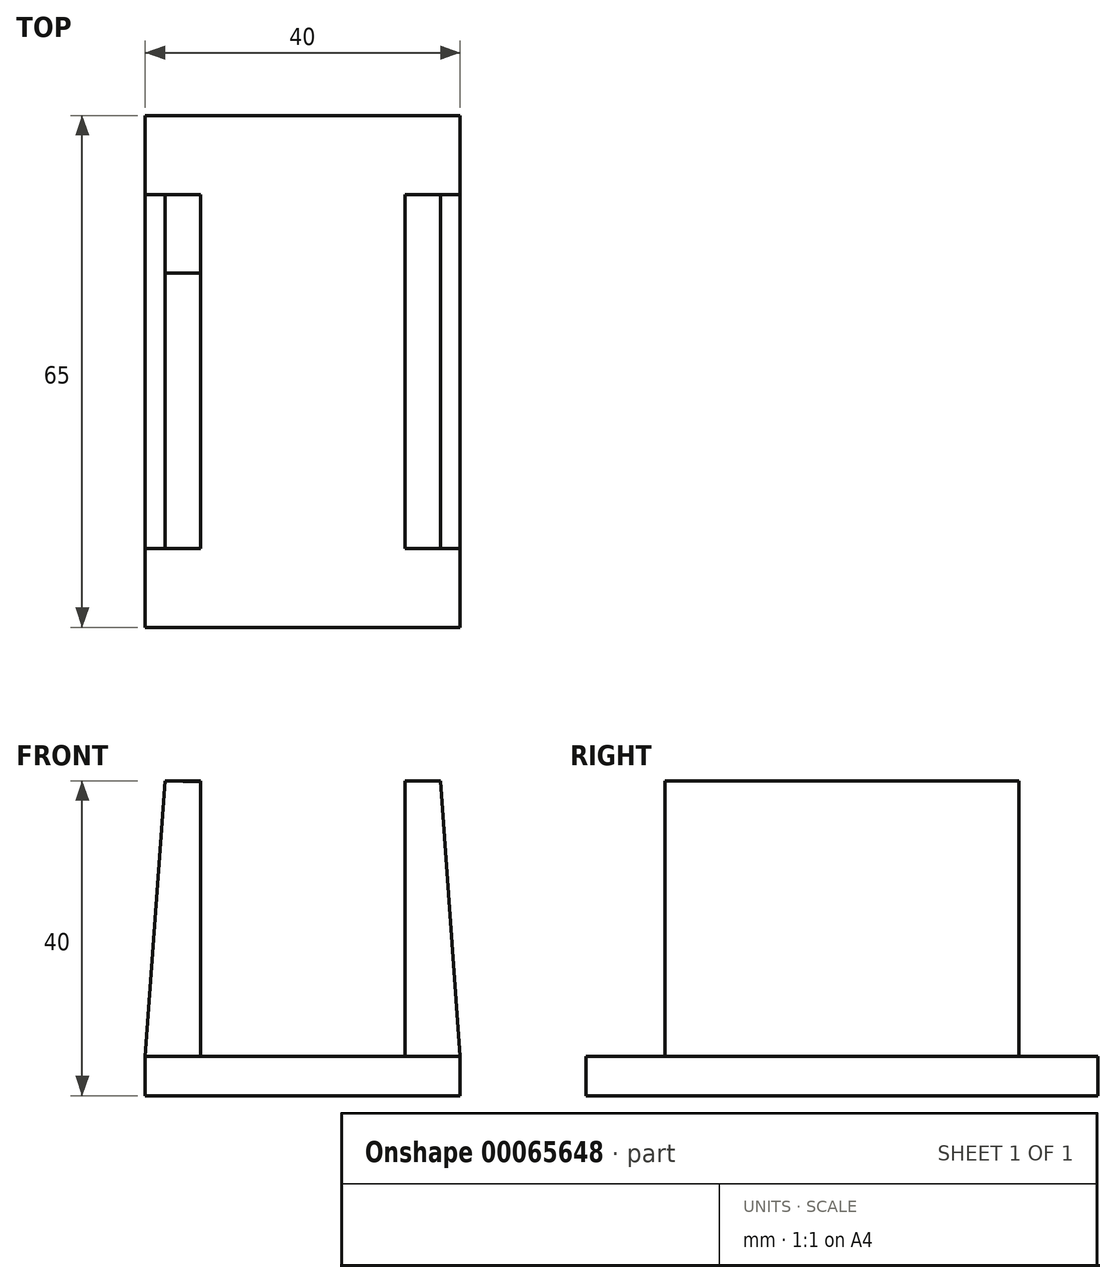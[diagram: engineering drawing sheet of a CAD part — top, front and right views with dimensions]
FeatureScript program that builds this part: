
annotation { "Feature Type Name" : "Feature", "Feature Type Description" : "" }
export const myFeature = defineFeature(function(context is Context, id is Id, definition is map)
    precondition{}
    {
        {
            var Q0;
            Q0=qCreatedBy(makeId("Top.planeOp"),FACE);
            var sketch = newSketch(context, id + "F0", { "sketchPlane" : qUnion([Q0])});
            skLineSegment(sketch, "E0.bottom", {"start": v(-22.03, 31.78) * mm, "end": v(17.97, 31.78) * mm});
            skLineSegment(sketch, "E0.top", {"start": v(-22.03, -33.22) * mm, "end": v(17.97, -33.22) * mm});
            skLineSegment(sketch, "E0.left", {"start": v(-22.03, 31.78) * mm, "end": v(-22.03, -33.22) * mm});
            skLineSegment(sketch, "E0.right", {"start": v(17.97, 31.78) * mm, "end": v(17.97, -33.22) * mm});
            skSolve(sketch);
        }
        {
            var Q0;
            Q0 = qSketchRegion(id + "F0", true);
            extrude(context, id + "F1", {"entities" : qUnion([Q0]), "depth" : 5 * mm});
        }
        {
            var Q0;
            Q0=makeQuery(id+"F1.opExtrude","SWEPT_FACE",FACE,{"disambiguationData":[OSD([sQuery(id+"F0.wireOp",EDGE,"E0.bottom")])]});
            cPlane(context, id + "F2", {"entities" : qUnion([Q0]), "cplaneType" : CPlaneType.OFFSET, "offset" : 10 * mm, "oppositeDirection" : true, "width" : 152.4 * mm, "height" : 152.4 * mm});
        }
        {
            var Q0;
            Q0=makeQuery(id+"F1.opExtrude","SWEPT_FACE",FACE,{"disambiguationData":[OSD([sQuery(id+"F0.wireOp",EDGE,"E0.top")])]});
            cPlane(context, id + "F3", {"entities" : qUnion([Q0]), "cplaneType" : CPlaneType.OFFSET, "offset" : 10 * mm, "oppositeDirection" : true, "width" : 152.4 * mm, "height" : 152.4 * mm});
        }
        {
            var Q0;
            Q0=qCreatedBy(id+"F2.planeOp",FACE);
            var sketch = newSketch(context, id + "F4", { "sketchPlane" : qUnion([Q0])});
            skLineSegment(sketch, "E1.bottom", {"start": v(-17.97, 5) * mm, "end": v(22.03, 5) * mm});
            skLineSegment(sketch, "E1.top", {"start": v(-15.47, 40) * mm, "end": v(19.53, 40) * mm});
            skLineSegment(sketch, "E1.left", {"start": v(-17.97, 5) * mm, "end": v(-15.47, 40) * mm});
            skLineSegment(sketch, "E1.right", {"start": v(22.03, 5) * mm, "end": v(19.53, 40) * mm});
            skPoint(sketch, "E2.0", {"position": v(-17.97, 5) * mm});
            skPoint(sketch, "E3.0", {"position": v(22.03, 5) * mm});
            skPoint(sketch, "E4", {"position": v(2.03, 40) * mm});
            skPoint(sketch, "E5", {"position": v(2.03, 5) * mm});
            skLineSegment(sketch, "E6", {"start": v(2.03, 40) * mm, "end": v(2.03, 5) * mm, "construction": true});
            skSolve(sketch);
        }
        {
            var Q0;
            Q0=makeQuery(id+"F4.imprint","IMPRINT",FACE,{"disambiguationData":[TD([[makeQuery(id+"F4.imprint","IMPRINT",EDGE,{"derivedFrom":sQuery(id+"F4.wireOp",EDGE,"E1.bottom")}),1.0]])]});
            var sketch = newSketch(context, id + "F5", { "sketchPlane" : qUnion([Q0])});
            skLineSegment(sketch, "E7.top", {"start": v(-10.97, 5) * mm, "end": v(15.03, 5) * mm});
            skPoint(sketch, "E8", {"position": v(2.03, 5) * mm});
            skLineSegment(sketch, "E9", {"start": v(-10.97, 39.84) * mm, "end": v(-10.97, 5) * mm});
            skLineSegment(sketch, "E10", {"start": v(15.03, 40.2) * mm, "end": v(15.03, 5) * mm});
            skLineSegment(sketch, "E11", {"start": v(-17.97, 5) * mm, "end": v(-15.47, 40) * mm});
            skLineSegment(sketch, "E12", {"start": v(-17.97, 5) * mm, "end": v(22.03, 5) * mm});
            skLineSegment(sketch, "E13", {"start": v(22.03, 5) * mm, "end": v(19.53, 40) * mm});
            skLineSegment(sketch, "E14", {"start": v(15.03, 40) * mm, "end": v(19.53, 40) * mm});
            skLineSegment(sketch, "E15", {"start": v(-15.47, 40) * mm, "end": v(-10.97, 39.84) * mm});
            skSolve(sketch);
        }
        {
            var Q0;
            Q0 = qSketchRegion(id + "F5", true);
            extrude(context, id + "F6", {"entities" : qUnion([Q0]), "operationType" : NewBodyOperationType.ADD, "oppositeDirection" : true, "depth" : 10 * mm});
        }
        {
            var Q0;
            Q0=qCreatedBy(id+"F3.planeOp",FACE);
            var sketch = newSketch(context, id + "F7", { "sketchPlane" : qUnion([Q0])});
            skLineSegment(sketch, "E16.top", {"start": v(-15.03, 5) * mm, "end": v(10.97, 5) * mm});
            skPoint(sketch, "E17", {"position": v(-2.03, 5) * mm});
            skLineSegment(sketch, "E18", {"start": v(-15.03, 39.84) * mm, "end": v(-15.03, 5) * mm});
            skLineSegment(sketch, "E19", {"start": v(10.97, 40.2) * mm, "end": v(10.97, 5) * mm});
            skLineSegment(sketch, "E20", {"start": v(-22.03, 5) * mm, "end": v(-19.53, 40) * mm});
            skLineSegment(sketch, "E21", {"start": v(-22.03, 5) * mm, "end": v(17.97, 5) * mm});
            skLineSegment(sketch, "E22", {"start": v(17.97, 5) * mm, "end": v(15.47, 40) * mm});
            skLineSegment(sketch, "E23", {"start": v(10.97, 40) * mm, "end": v(15.47, 40) * mm});
            skLineSegment(sketch, "E24", {"start": v(-19.53, 40) * mm, "end": v(-15.03, 39.84) * mm});
            skPoint(sketch, "E25.0", {"position": v(-22.03, 5) * mm});
            skPoint(sketch, "E26.0", {"position": v(17.97, 5) * mm});
            skSolve(sketch);
        }
        {
            var Q0;
            Q0 = qSketchRegion(id + "F7", true);
            extrude(context, id + "F8", {"entities" : qUnion([Q0]), "operationType" : NewBodyOperationType.ADD, "oppositeDirection" : true, "depth" : 45 * mm});
        }
    });
